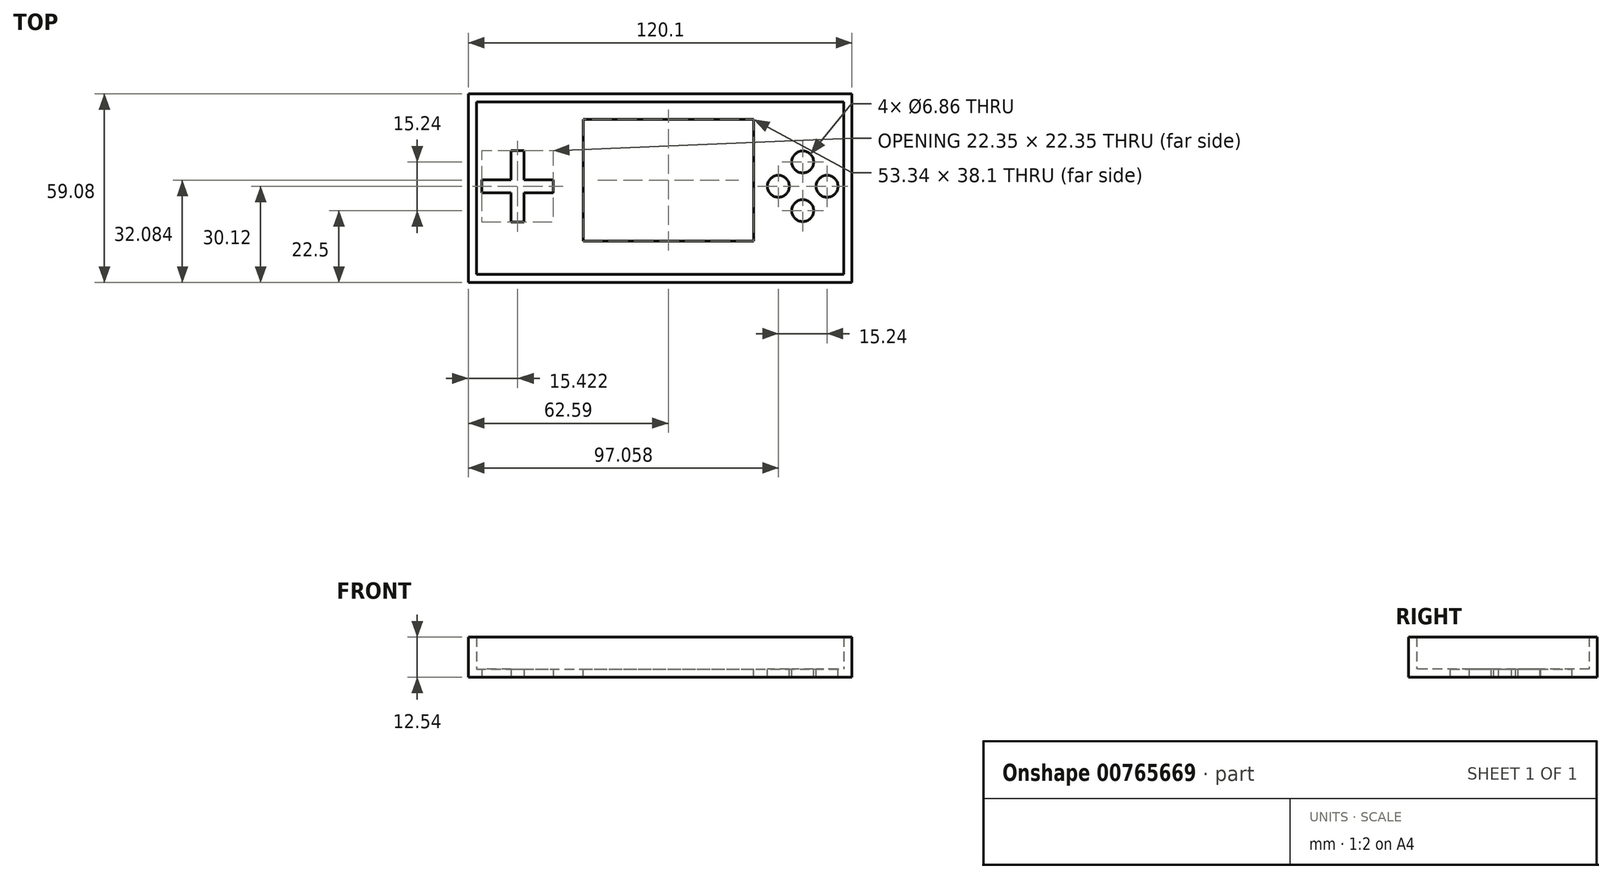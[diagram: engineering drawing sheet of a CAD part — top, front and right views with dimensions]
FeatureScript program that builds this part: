
annotation { "Feature Type Name" : "Feature", "Feature Type Description" : "" }
export const myFeature = defineFeature(function(context is Context, id is Id, definition is map)
    precondition{}
    {
        {
            var Q0;
            Q0=qCreatedBy(makeId("Top.planeOp"),FACE);
            var sketch = newSketch(context, id + "F0", { "sketchPlane" : qUnion([Q0])});
            skLineSegment(sketch, "E0.bottom", {"start": v(-56.27, 26.42) * mm, "end": v(58.75, 26.42) * mm});
            skLineSegment(sketch, "E0.top", {"start": v(-56.27, -27.58) * mm, "end": v(58.75, -27.58) * mm});
            skLineSegment(sketch, "E0.left", {"start": v(-56.27, 26.42) * mm, "end": v(-56.27, -27.58) * mm});
            skLineSegment(sketch, "E0.right", {"start": v(58.75, 26.42) * mm, "end": v(58.75, -27.58) * mm});
            skSolve(sketch);
        }
        {
            var Q0;
            Q0 = qSketchRegion(id + "F0", true);
            extrude(context, id + "F1", {"entities" : qUnion([Q0]), "depth" : 10 * mm, "offsetDistance" : 25.4 * mm});
        }
        {
            var Q0;
            Q0=makeQuery(id+"F1.opExtrude","CAP_FACE",FACE,{"disambiguationData":[OSD([sQuery(id+"F0.wireOp",EDGE,"E0.bottom"),sQuery(id+"F0.wireOp",EDGE,"E0.top"),sQuery(id+"F0.wireOp",EDGE,"E0.left"),sQuery(id+"F0.wireOp",EDGE,"E0.right")])],"isStart":false});
            shell(context, id + "F2", {"entities" : qUnion([Q0]), "thickness" : 2.54 * mm, "oppositeDirection" : true});
        }
        {
            var Q0;
            Q0=makeQuery(id+"F1.opExtrude","CAP_FACE",FACE,{"disambiguationData":[OSD([sQuery(id+"F0.wireOp",EDGE,"E0.bottom"),sQuery(id+"F0.wireOp",EDGE,"E0.top"),sQuery(id+"F0.wireOp",EDGE,"E0.left"),sQuery(id+"F0.wireOp",EDGE,"E0.right")])],"isStart":true});
            var sketch = newSketch(context, id + "F3", { "sketchPlane" : qUnion([Q0])});
            skLineSegment(sketch, "E1.bottom", {"start": v(-22.9, 17.09) * mm, "end": v(30.45, 17.09) * mm});
            skLineSegment(sketch, "E1.top", {"start": v(-22.9, -21.01) * mm, "end": v(30.45, -21.01) * mm});
            skLineSegment(sketch, "E1.left", {"start": v(-22.9, 17.09) * mm, "end": v(-22.9, -21.01) * mm});
            skLineSegment(sketch, "E1.right", {"start": v(30.45, 17.09) * mm, "end": v(30.45, -21.01) * mm});
            skSolve(sketch);
        }
        {
            var Q0;
            Q0 = qSketchRegion(id + "F3", true);
            extrude(context, id + "F4", {"entities" : qUnion([Q0]), "operationType" : NewBodyOperationType.REMOVE, "endBound" : BoundingType.SYMMETRIC, "depth" : 25.4 * mm, "offsetDistance" : 25.4 * mm});
        }
        {
            var Q0;
            Q0=qCreatedBy(makeId("Top.planeOp"),FACE);
            var sketch = newSketch(context, id + "F5", { "sketchPlane" : qUnion([Q0])});
            skLineSegment(sketch, "E2", {"start": v(-45.42, -11.18) * mm, "end": v(-41.36, -11.18) * mm});
            skLineSegment(sketch, "E3", {"start": v(-41.36, -11.18) * mm, "end": v(-41.36, -2.03) * mm});
            skLineSegment(sketch, "E4", {"start": v(-41.36, -2.03) * mm, "end": v(-32.21, -2.03) * mm});
            skLineSegment(sketch, "E5", {"start": v(-32.21, -2.03) * mm, "end": v(-32.21, 2.03) * mm});
            skLineSegment(sketch, "E6", {"start": v(-32.21, 2.03) * mm, "end": v(-41.36, 2.03) * mm});
            skLineSegment(sketch, "E7", {"start": v(-41.36, 2.03) * mm, "end": v(-41.36, 11.18) * mm});
            skLineSegment(sketch, "E8", {"start": v(-41.36, 11.18) * mm, "end": v(-45.42, 11.18) * mm});
            skLineSegment(sketch, "E9", {"start": v(-45.42, 11.18) * mm, "end": v(-45.42, 2.03) * mm});
            skLineSegment(sketch, "E10", {"start": v(-45.42, 2.03) * mm, "end": v(-54.56, 2.03) * mm});
            skLineSegment(sketch, "E11", {"start": v(-54.56, 2.03) * mm, "end": v(-54.56, -2.03) * mm});
            skLineSegment(sketch, "E12", {"start": v(-54.56, -2.03) * mm, "end": v(-45.42, -2.03) * mm});
            skLineSegment(sketch, "E13", {"start": v(-45.42, -11.18) * mm, "end": v(-45.42, -2.03) * mm});
            skPoint(sketch, "E14", {"position": v(-32.21, 0) * mm});
            skLineSegment(sketch, "E15", {"start": v(0, 0) * mm, "end": v(-30.92, 0) * mm, "construction": true});
            skSolve(sketch);
        }
        {
            var Q0;
            Q0 = qSketchRegion(id + "F5", true);
            extrude(context, id + "F6", {"entities" : qUnion([Q0]), "operationType" : NewBodyOperationType.REMOVE, "endBound" : BoundingType.SYMMETRIC, "depth" : 25.4 * mm, "offsetDistance" : 25.4 * mm});
        }
        {
            var Q0;
            Q0=qCreatedBy(makeId("Top.planeOp"),FACE);
            var sketch = newSketch(context, id + "F7", { "sketchPlane" : qUnion([Q0])});
            skLineSegment(sketch, "E16", {"start": v(0, 0) * mm, "end": v(45.87, 0) * mm, "construction": true});
            skLineSegment(sketch, "E17", {"start": v(45.87, -27.46) * mm, "end": v(45.87, 26.34) * mm, "construction": true});
            skCircle(sketch, "E18", {"center": v(45.87, -7.62) * mm, "radius": 3.43 * mm});
            skCircle(sketch, "E19", {"center": v(53.49, 0) * mm, "radius": 3.43 * mm});
            skCircle(sketch, "E20", {"center": v(45.87, 7.62) * mm, "radius": 3.43 * mm});
            skCircle(sketch, "E21", {"center": v(38.25, 0) * mm, "radius": 3.43 * mm});
            skSolve(sketch);
        }
        {
            var Q0;
            Q0 = qSketchRegion(id + "F7", true);
            extrude(context, id + "F8", {"entities" : qUnion([Q0]), "operationType" : NewBodyOperationType.REMOVE, "endBound" : BoundingType.SYMMETRIC, "oppositeDirection" : true, "depth" : 25.4 * mm, "offsetDistance" : 25.4 * mm});
        }
    });
